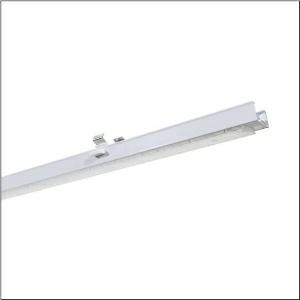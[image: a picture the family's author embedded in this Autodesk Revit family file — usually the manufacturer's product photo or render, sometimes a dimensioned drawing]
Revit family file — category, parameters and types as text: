
# Revit family: sanierungs-leuchteneinsatz_31_gen_2_51re14mb4cb_c25e
name_source: partatom
category: Lighting Fixtures
units: mm (PartAtom-declared; Revit-internal decimal feet)

## family parameters
Cut with Voids When Loaded = No
Host = Face
Light Source = No
Part Type = Normal
Room Calculation Point = No
Round Connector Dimension = Use Diameter
Shared = No

## types (1)
- --- (1 x LED, 11500 lm, 66 W, 4000K)
    Apparent Load = 66 VA
    CIE Flux Codes = 72 92 98 99 100
    Color Rendering = 80
    Color Temperature = 4000K
    Default Elevation = 1800 mm
    Description = Refurbishment luminaire insert Gen.2, luminaire insert, of extruded aluminium section, coated, traffic white (RAL 9016), length: 1.472mm, width: 91mm, height: 53mm, LED rated luminous flux: 11.500lm, light colour: 840, control gear: ON/OFF Multilumen, control gear: ECG Multilumen, with system connector: socket, mains connection: 220..240V, AC, 50/60Hz, connected load according to luminous flux setting (19/24/32/37/47/52/60/66W), luminous flux adjustable on luminaire in eight steps (3450/4380/5800/6700/8350/9200/10500/11500lm ), primary light control with lens, of plastic, primary optical cover: cover, of PMMA, light emission: direct distribution, primary light characteristic: asymmetric, protection rating (complete): IP20, insulation class (complete): insulation class I (protective earthing), certification: CE, UKCA, permissible ambient temperature for indoor applications: -20..+40°C, packaging unit: 1 piece
    Height = 58 mm
    Lamp = 1 x LED
    Lamp Light Flux = 11500 lm
    Lamp Power = 66 W
    Lamp count = 1
    Length = 1472 mm
    Luminous efficacy = 174 lm/W
    Manufacturer = Siteco
    ModVariant = No
    Model = 51RE14MB4CB
    Mounting Place = Ceiling
    Mounting Type = Pendant
    Number of Poles = 1
    OnlyDefault = Yes
    Power Factor = 1
    Product Name = Sanierungs-Leuchteneinsatz 31 Gen.2
    Product group = luminaire insert
    ProductGroupID = 902
    Protection Class = Protection class I
    Protection Degree = IP 20
    RLX_Detail_Level = 1
    RlxData = <blob elided: 21877 chars, md5=1b598bf7>
    Socket = socket
    Standby Power = 0 W
    System Light Flux = 11500 lm
    System Power = 66 W
    Type Comments = factory setting: luminous flux: 100 % | (ON | ON | ON)
    Type Image = l_1266702.jpg
    URL = http://relux.com
    VarID = @adj_068009
    Voltage = 0 V
    Weight = 0.00 kg
    Width = 65 mm

## geometry (parser evidence)
native form markers: Blend x4, Sweep x10
no freeform markers — native parametric forms only
